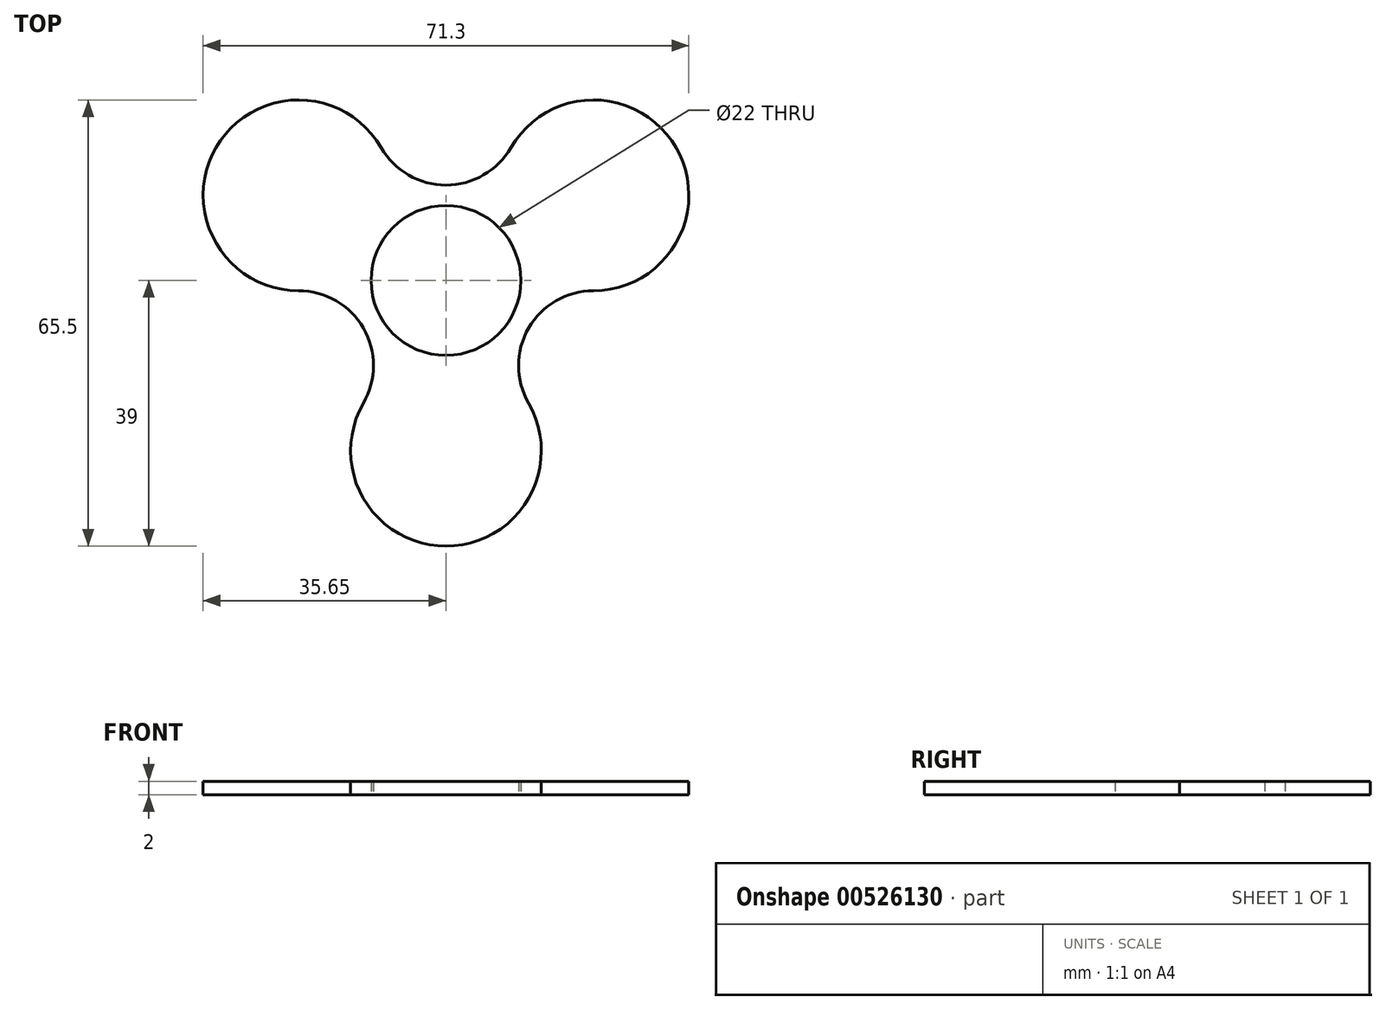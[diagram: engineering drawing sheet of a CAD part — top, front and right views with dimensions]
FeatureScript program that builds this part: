
annotation { "Feature Type Name" : "Feature", "Feature Type Description" : "" }
export const myFeature = defineFeature(function(context is Context, id is Id, definition is map)
    precondition{}
    {
        {
            var Q0;
            Q0=qCreatedBy(makeId("Top.planeOp"),FACE);
            var sketch = newSketch(context, id + "F0", { "sketchPlane" : qUnion([Q0])});
            skArc(sketch, "E0", {"start": v(-9.53, 19.5) * mm, "mid": v(0, 14) * mm, "end": v(9.53, 19.5) * mm});
            skArc(sketch, "E1.2.0", {"start": v(-12.12, -18) * mm, "mid": v(-12.12, -7) * mm, "end": v(-21.65, -1.5) * mm});
            skArc(sketch, "E1.4.0", {"start": v(21.65, -1.5) * mm, "mid": v(12.12, -7) * mm, "end": v(12.12, -18) * mm});
            skPoint(sketch, "E1.center", {"position": v(0, 0) * mm});
            skArc(sketch, "E2.1.0", {"start": v(-9.53, 19.5) * mm, "mid": v(-33.77, 19.5) * mm, "end": v(-21.65, -1.5) * mm});
            skArc(sketch, "E2.3.0", {"start": v(-12.12, -18) * mm, "mid": v(0, -39) * mm, "end": v(12.12, -18) * mm});
            skArc(sketch, "E2.5.0", {"start": v(21.65, -1.5) * mm, "mid": v(33.77, 19.5) * mm, "end": v(9.53, 19.5) * mm});
            skCircle(sketch, "E3", {"center": v(0, 0) * mm, "radius": 11 * mm});
            skSolve(sketch);
        }
        {
            var Q0;
            Q0 = qSketchRegion(id + "F0", true);
            extrude(context, id + "F1", {"entities" : qUnion([Q0]), "depth" : 2 * mm, "offsetDistance" : 25 * mm});
        }
    });
